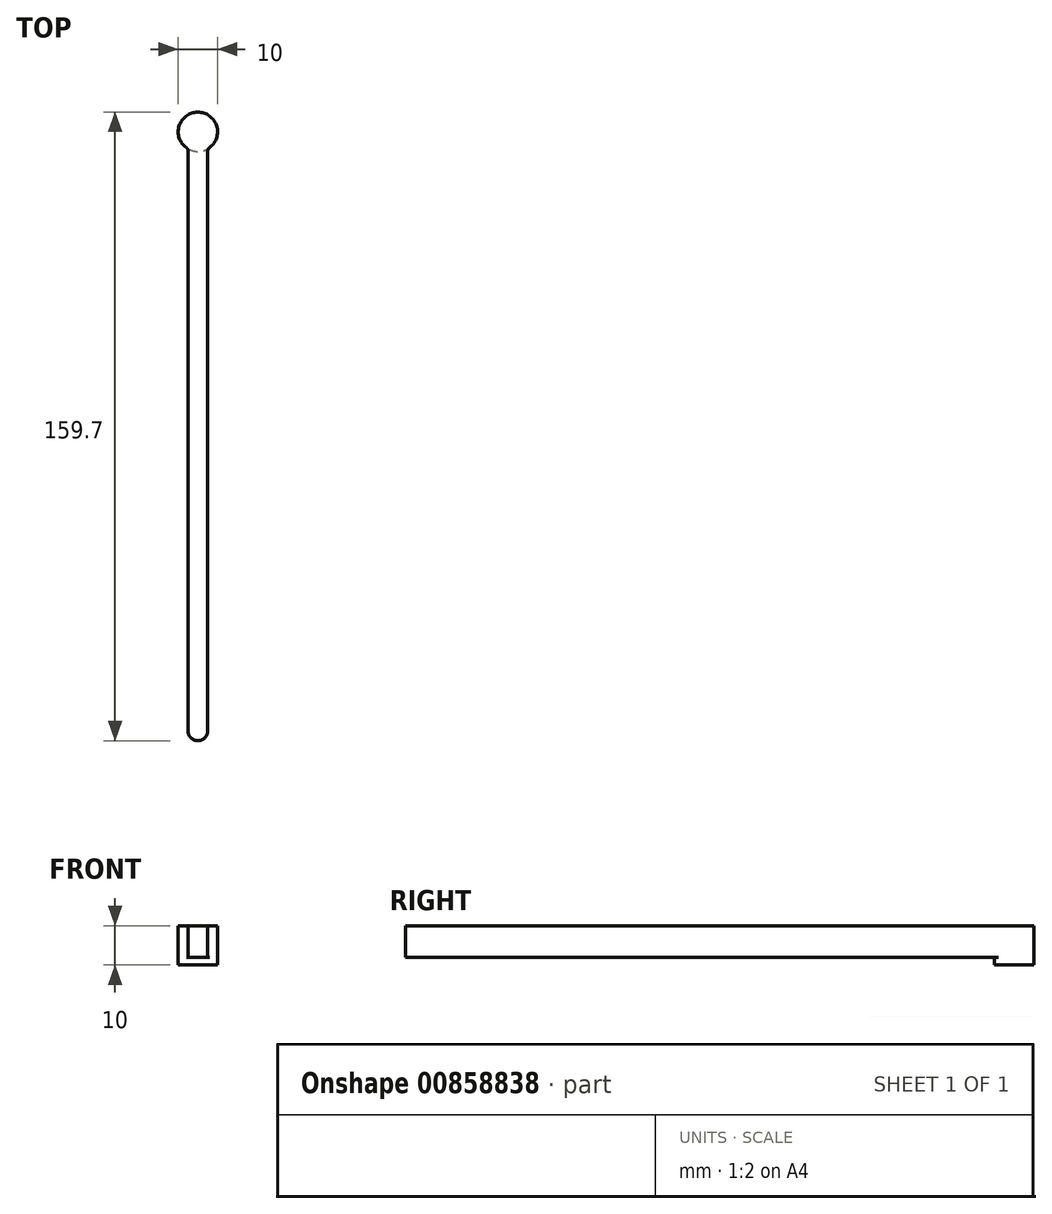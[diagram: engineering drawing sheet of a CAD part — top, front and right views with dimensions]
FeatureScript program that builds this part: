
annotation { "Feature Type Name" : "Feature", "Feature Type Description" : "" }
export const myFeature = defineFeature(function(context is Context, id is Id, definition is map)
    precondition{}
    {
        {
            var Q0;
            Q0=qCreatedBy(makeId("Top.planeOp"),FACE);
            var sketch = newSketch(context, id + "F0", { "sketchPlane" : qUnion([Q0])});
            skCircle(sketch, "E0", {"center": v(0, 0) * mm, "radius": 11.25 * mm});
            skCircle(sketch, "E1", {"center": v(0, 0) * mm, "radius": 50 * mm});
            skCircle(sketch, "E2", {"center": v(0, 0) * mm, "radius": 27.68 * mm, "construction": true});
            skCircle(sketch, "E3", {"center": v(-26.58, -7.75) * mm, "radius": 5 * mm});
            skPoint(sketch, "E4.orphan", {"position": v(-30.87, -2.38) * mm});
            skPoint(sketch, "E5.orphan", {"position": v(-33.37, -6.71) * mm});
            skArc(sketch, "E6", {"start": v(-46.48, 10.85) * mm, "mid": v(-38.36, 3) * mm, "end": v(-29.08, -3.42) * mm});
            skLineSegment(sketch, "E7.1.0", {"start": v(17.5, -171.34) * mm, "end": v(17.5, -23.47) * mm});
            skLineSegment(sketch, "E7.1.1", {"start": v(20, -24.14) * mm, "end": v(20, -173.85) * mm, "construction": true});
            skLineSegment(sketch, "E7.1.2", {"start": v(22.5, -171.34) * mm, "end": v(22.5, -23.47) * mm});
            skArc(sketch, "E7.1.3", {"start": v(17.5, -171.34) * mm, "mid": v(20, -173.84) * mm, "end": v(22.5, -171.34) * mm});
            skLineSegment(sketch, "E7.1.4", {"start": v(17.5, -171.34) * mm, "end": v(22.5, -171.34) * mm});
            skArc(sketch, "E7.1.5", {"start": v(13.85, -45.67) * mm, "mid": v(16.58, -34.72) * mm, "end": v(17.5, -23.47) * mm});
            skCircle(sketch, "E7.1.6", {"center": v(20, -19.14) * mm, "radius": 5 * mm});
            skArc(sketch, "E7.2.5", {"start": v(32.63, 34.83) * mm, "mid": v(21.78, 31.72) * mm, "end": v(11.58, 26.9) * mm});
            skCircle(sketch, "E7.2.6", {"center": v(6.58, 26.9) * mm, "radius": 5 * mm});
            skArc(sketch, "E8", {"start": v(-39.47, 17.95) * mm, "mid": v(-46.28, 17.66) * mm, "end": v(-46.48, 10.85) * mm});
            skArc(sketch, "E9", {"start": v(23.73, 39.68) * mm, "mid": v(24.98, 41.88) * mm, "end": v(23.66, 44.05) * mm});
            skPoint(sketch, "E10.orphan", {"position": v(-48.28, 12.99) * mm});
            skArc(sketch, "E11", {"start": v(-39.47, 17.95) * mm, "mid": v(-34.24, 15.99) * mm, "end": v(-28.98, 17.84) * mm});
            skLineSegment(sketch, "E12", {"start": v(-28.98, 17.84) * mm, "end": v(2.28, 43.55) * mm});
            skArc(sketch, "E13", {"start": v(19.5, 46.04) * mm, "mid": v(10.54, 47.2) * mm, "end": v(2.28, 43.55) * mm});
            skArc(sketch, "E14.1.1", {"start": v(4.2, -43.15) * mm, "mid": v(7.85, -48.9) * mm, "end": v(13.85, -45.67) * mm});
            skArc(sketch, "E14.1.2", {"start": v(4.2, -43.15) * mm, "mid": v(3.28, -37.65) * mm, "end": v(-0.96, -34.02) * mm});
            skLineSegment(sketch, "E14.1.3", {"start": v(-0.96, -34.02) * mm, "end": v(-38.85, -19.8) * mm});
            skArc(sketch, "E14.1.4", {"start": v(-49.62, -6.13) * mm, "mid": v(-46.15, -14.47) * mm, "end": v(-38.85, -19.8) * mm});
            skArc(sketch, "E14.1.5", {"start": v(-46.23, 0.7) * mm, "mid": v(-48.76, 0.69) * mm, "end": v(-49.98, -1.53) * mm});
            skArc(sketch, "E14.2.1", {"start": v(35.28, 25.2) * mm, "mid": v(38.43, 31.25) * mm, "end": v(32.63, 34.83) * mm});
            skArc(sketch, "E14.2.2", {"start": v(35.28, 25.2) * mm, "mid": v(30.97, 21.66) * mm, "end": v(29.94, 16.18) * mm});
            skLineSegment(sketch, "E14.2.3", {"start": v(29.94, 16.18) * mm, "end": v(36.57, -23.75) * mm});
            skArc(sketch, "E14.2.4", {"start": v(30.12, -39.9) * mm, "mid": v(35.6, -32.73) * mm, "end": v(36.57, -23.75) * mm});
            skArc(sketch, "E14.2.5", {"start": v(22.5, -40.39) * mm, "mid": v(23.78, -42.57) * mm, "end": v(26.32, -42.51) * mm});
            skPoint(sketch, "E15.orphan", {"position": v(35.4, 35.32) * mm});
            skPoint(sketch, "E16.orphan", {"position": v(12.9, -48.3) * mm});
            skSolve(sketch);
        }
        {
            var Q0;
            {var subQ0=sQuery(id+"F0.wireOp",EDGE,"E7.1.6");var subQ2=makeQuery(id+"F0.imprint","INTERSECT",VERTEX,{"derivedFrom":[sQuery(id+"F0.wireOp",EDGE,"E7.1.2"),subQ0]});Q0=makeQuery(id+"F0.imprint","IMPRINT",FACE,{"disambiguationData":[TD([[makeQuery(id+"F0.imprint","IMPRINT",EDGE,{"disambiguationData":[TD([[subQ2,1.0]])],"derivedFrom":subQ0}),1.0]])]});}
            var Q1;
            {var subQ4=sQuery(id+"F0.wireOp",EDGE,"E1");var subQ6=sQuery(id+"F0.wireOp",EDGE,"E7.1.0");var subQ8=makeQuery(id+"F0.imprint","INTERSECT",VERTEX,{"derivedFrom":[subQ4,subQ6]});Q1=makeQuery(id+"F0.imprint","IMPRINT",FACE,{"disambiguationData":[TD([[makeQuery(id+"F0.imprint","IMPRINT",EDGE,{"disambiguationData":[TD([[subQ8,-1.0]])],"derivedFrom":subQ4}),1.0]])]});}
            var Q2;
            {var subQ5=sQuery(id+"F0.wireOp",EDGE,"E7.1.4");Q2=makeQuery(id+"F0.imprint","IMPRINT",FACE,{"disambiguationData":[TD([[makeQuery(id+"F0.imprint","IMPRINT",EDGE,{"derivedFrom":subQ5}),1.0]])]});}
            var Q3;
            Q3=makeQuery(id+"F0.imprint","IMPRINT",FACE,{"disambiguationData":[TD([[makeQuery(id+"F0.imprint","IMPRINT",EDGE,{"derivedFrom":sQuery(id+"F0.wireOp",EDGE,"E7.1.3")}),1.0]])]});
            extrude(context, id + "F1", {"entities" : qUnion([Q0, Q1, Q2, Q3]), "depth" : 8 * mm, "offsetDistance" : 25 * mm});
        }
        {
            var Q0;
            {var subQ0=sQuery(id+"F0.wireOp",EDGE,"E7.1.6");var subQ2=makeQuery(id+"F0.imprint","INTERSECT",VERTEX,{"derivedFrom":[sQuery(id+"F0.wireOp",EDGE,"E7.1.2"),subQ0]});Q0=makeQuery(id+"F0.imprint","IMPRINT",FACE,{"disambiguationData":[TD([[makeQuery(id+"F0.imprint","IMPRINT",EDGE,{"disambiguationData":[TD([[subQ2,1.0]])],"derivedFrom":subQ0}),1.0]])]});}
            extrude(context, id + "F2", {"entities" : qUnion([Q0]), "operationType" : NewBodyOperationType.ADD, "oppositeDirection" : true, "depth" : 2 * mm, "offsetDistance" : 25 * mm});
        }
        {
            var Q0;
            Q0=makeQuery(id+"F1.opExtrude","SWEPT_EDGE",EDGE,{"disambiguationData":[OSD([sQuery(id+"F0.wireOp",EDGE,"E7.1.0"),sQuery(id+"F0.wireOp",EDGE,"E7.1.6"),sQuery(id+"F0.wireOp",EDGE,"E7.1.5")])]});
            var Q1;
            Q1=makeQuery(id+"F1.opExtrude","SWEPT_EDGE",EDGE,{"disambiguationData":[OSD([sQuery(id+"F0.wireOp",EDGE,"E7.1.2"),sQuery(id+"F0.wireOp",EDGE,"E7.1.6")])]});
            fillet(context, id + "F3", {"entities" : qUnion([Q0, Q1]), "radius" : 1 * mm, "tangentPropagation" : true, "allowEdgeOverflow" : false});
        }
    });
